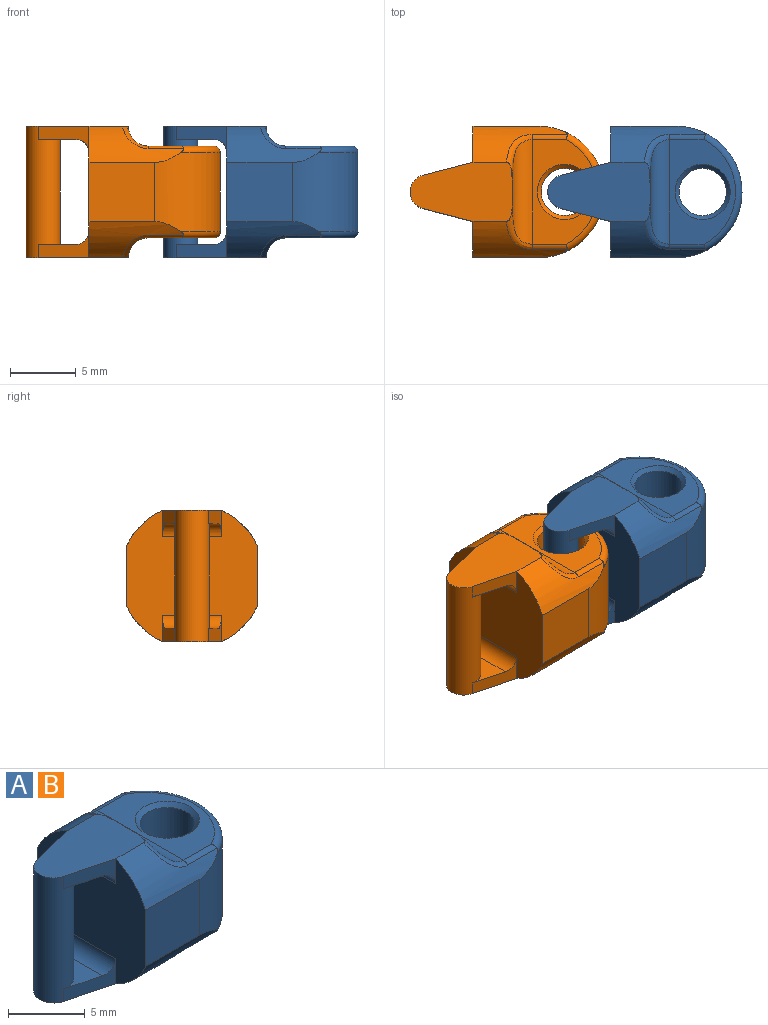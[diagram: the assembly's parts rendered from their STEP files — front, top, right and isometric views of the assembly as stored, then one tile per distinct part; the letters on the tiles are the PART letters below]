
ASSEMBLY  parts=2 mates=3
PART A: 34 faces, bbox 21.2x16x19 mm
  f0: plane 5x4.5mm, normal (0,-1,0), area 22.5mm2, adj f1,f31,f32,f33
  f1: plane 10x10mm, normal (-1,0,0), area 70.6mm2, adj f0,f2,f23,f24,f25,f26,f27,f28
  f2: cylinder r=5.48mm len=7.2mm, axis (-1,0,0), area 15.9mm2, adj f1,f3,f20,f21,f22,f23,f32
  f3: torus R=4.5mm, axis (0,0,-1), area 8.4mm2, adj f2,f4,f19,f22,f32,f33
  f4: plane 13.96x11mm, normal (0,0,-1), area 20.5mm2, adj f3,f5,f6,f19,f22
  f5: cylinder r=1.5mm len=7.96mm, axis (0,1,0), area 0mm2, adj f4,f21
  f6: cone r=2.1mm half-angle=45deg, axis (0,0,-1), area 5.2mm2, adj f4,f7
  f7: cylinder r=1.8mm len=6.4mm, axis (0,0,-1), area 72.4mm2, adj f6,f8
  f8: cone r=1.8mm half-angle=45deg, axis (0,0,1), area 5.2mm2, adj f7,f9
  f9: plane 13.96x11mm, normal (0,0,1), area 20.5mm2, adj f8,f10,f16,f17,f18
  f10: cylinder r=0.5mm len=2.7mm, axis (-1,0,0), area 1.2mm2, adj f9,f11,f16,f24
  f11: bspline ~8.76x2.18mm, area 4.3mm2, adj f10,f12,f17,f18,f24,f31
  f12: plane 7.8x4.5mm, normal (0,0,1), area 28.5mm2, adj f11,f13,f24,f25,f27,f31
  f13: cylinder r=1.3mm len=10mm, axis (0,0,-1), area 72.2mm2, adj f12,f14,f15,f20,f25,f27,f28,f30
  f14: plane 3.98x2.83mm, normal (0,0,-1), area 5.7mm2, adj f13,f25,f26,f27
  f15: plane 3.98x2.83mm, normal (0,0,1), area 5.7mm2, adj f13,f28,f29,f30
  f16: torus R=4.5mm, axis (0,0,-1), area 8.4mm2, adj f9,f10,f17,f24,f31,f32
  f17: cylinder r=0.5mm len=2.7mm, axis (-1,0,0), area 1.2mm2, adj f9,f11,f16,f31
  f18: cylinder r=1.5mm len=7.96mm, axis (0,1,0), area 0mm2, adj f9,f11
  f19: cylinder r=0.5mm len=2.7mm, axis (-1,0,0), area 1.2mm2, adj f3,f4,f21,f33
  f20: plane 7.8x4.5mm, normal (0,0,-1), area 28.5mm2, adj f2,f13,f21,f28,f30,f33
  f21: bspline ~8.76x2.18mm, area 4.3mm2, adj f2,f5,f19,f20,f22,f33
  f22: cylinder r=0.5mm len=2.7mm, axis (-1,0,0), area 1.2mm2, adj f2,f3,f4,f21
  f23: plane 5x4.5mm, normal (0,1,0), area 22.5mm2, adj f1,f2,f24,f32
  f24: cylinder r=5.48mm len=7.2mm, axis (-1,0,0), area 15.9mm2, adj f1,f10,f11,f12,f16,f23,f32
  f25: plane 3.94x2.11mm, normal (-0.25,0.97,0), area 4.2mm2, adj f1,f12,f13,f14,f26
  f26: cylinder r=1mm len=4.5mm, axis (0,-1,0), area 6.7mm2, adj f1,f14,f25,f27
  f27: plane 3.94x2.11mm, normal (-0.25,-0.97,0), area 4.2mm2, adj f1,f12,f13,f14,f26
  f28: plane 3.94x2.11mm, normal (-0.25,-0.97,0), area 4.2mm2, adj f1,f13,f15,f20,f29
  f29: cylinder r=1mm len=4.5mm, axis (0,1,0), area 6.7mm2, adj f1,f15,f28,f30
  f30: plane 3.94x2.11mm, normal (-0.25,0.97,0), area 4.2mm2, adj f1,f13,f15,f20,f29
  f31: cylinder r=5.48mm len=7.2mm, axis (-1,0,0), area 15.9mm2, adj f0,f1,f11,f12,f16,f17,f32
  f32: cylinder r=5mm len=10mm, axis (0,0,-1), area 91.2mm2, adj f0,f2,f3,f16,f23,f24,f31,f33
  f33: cylinder r=5.48mm len=7.2mm, axis (-1,0,0), area 15.9mm2, adj f0,f1,f3,f19,f20,f21,f32
PART B: same geometry as A
PLACE A t=(10.23,-1.1,0.57)mm
PLACE B t=(-0.27,-1.1,0.57)mm fixed
MATE planar B.f0 <-> A.f0  axis (0,-1,0) through (-2.77,-6.1,0.57)mm
MATE cylindrical A.f13 <-> B.f6  axis (0,0,-1) through (1.73,-1.1,0.57)mm
MATE planar A.f14 <-> B.f14  axis (0,0,-1) through (3.42,-1.1,4.57)mm
